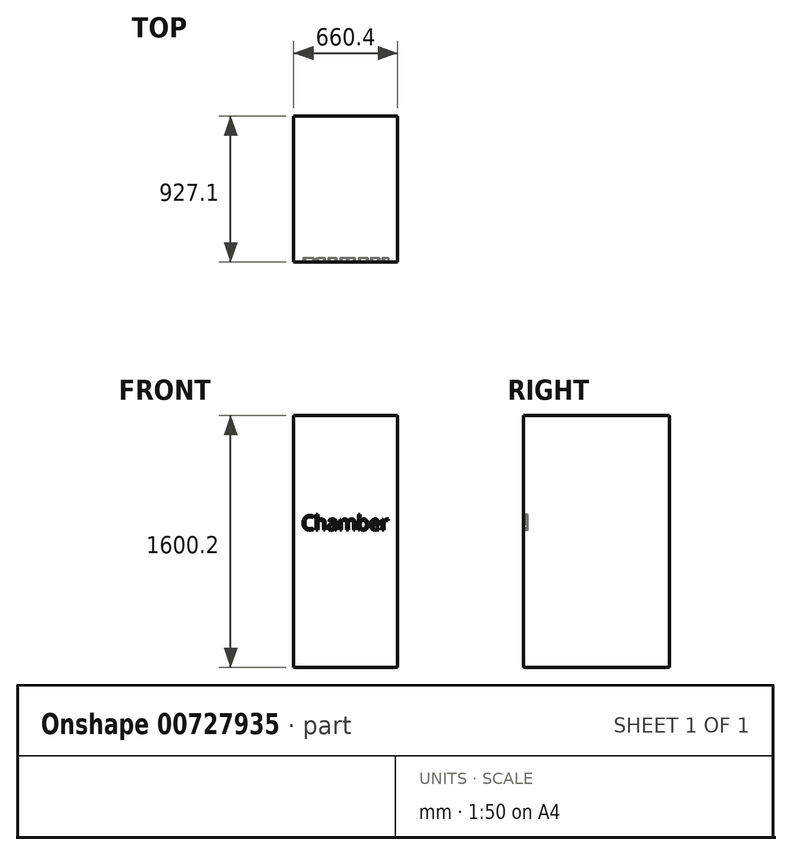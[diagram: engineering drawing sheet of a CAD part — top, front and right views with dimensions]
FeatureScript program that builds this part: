
annotation { "Feature Type Name" : "Feature", "Feature Type Description" : "" }
export const myFeature = defineFeature(function(context is Context, id is Id, definition is map)
    precondition{}
    {
        {
            var Q0;
            Q0=qCreatedBy(makeId("Top.planeOp"),FACE);
            var sketch = newSketch(context, id + "F0", { "sketchPlane" : qUnion([Q0])});
            skLineSegment(sketch, "E0.bottom", {"start": v(330.2, -463.55) * mm, "end": v(-330.2, -463.55) * mm});
            skLineSegment(sketch, "E0.top", {"start": v(330.2, 463.55) * mm, "end": v(-330.2, 463.55) * mm});
            skLineSegment(sketch, "E0.left", {"start": v(330.2, -463.55) * mm, "end": v(330.2, 463.55) * mm});
            skLineSegment(sketch, "E0.right", {"start": v(-330.2, -463.55) * mm, "end": v(-330.2, 463.55) * mm});
            skPoint(sketch, "E0.middle", {"position": v(0, 0) * mm});
            skSolve(sketch);
        }
        {
            var Q0;
            Q0 = qSketchRegion(id + "F0", true);
            extrude(context, id + "F1", {"entities" : qUnion([Q0]), "depth" : 1600.2 * mm, "offsetDistance" : 25.4 * mm});
        }
        {
            var Q0;
            Q0=makeQuery(id+"F1.opExtrude","SWEPT_FACE",FACE,{"disambiguationData":[OSD([sQuery(id+"F0.wireOp",EDGE,"E0.bottom")])]});
            var sketch = newSketch(context, id + "F2", { "sketchPlane" : qUnion([Q0])});
            skText(sketch, "E1", { "text": "Chamber", "fontName": "OpenSans-Regular.ttf"});
            const initialGuessF2  = {"E1": [-0.2794, 0.873, 1, 0, 0.0922]};
            skSetInitialGuess(sketch, initialGuessF2);
            skSolve(sketch);
        }
        {
            var Q0;
            Q0 = qSketchRegion(id + "F2", true);
            extrude(context, id + "F3", {"entities" : qUnion([Q0]), "operationType" : NewBodyOperationType.REMOVE, "oppositeDirection" : true, "depth" : 25.4 * mm, "offsetDistance" : 25.4 * mm});
        }
    });
